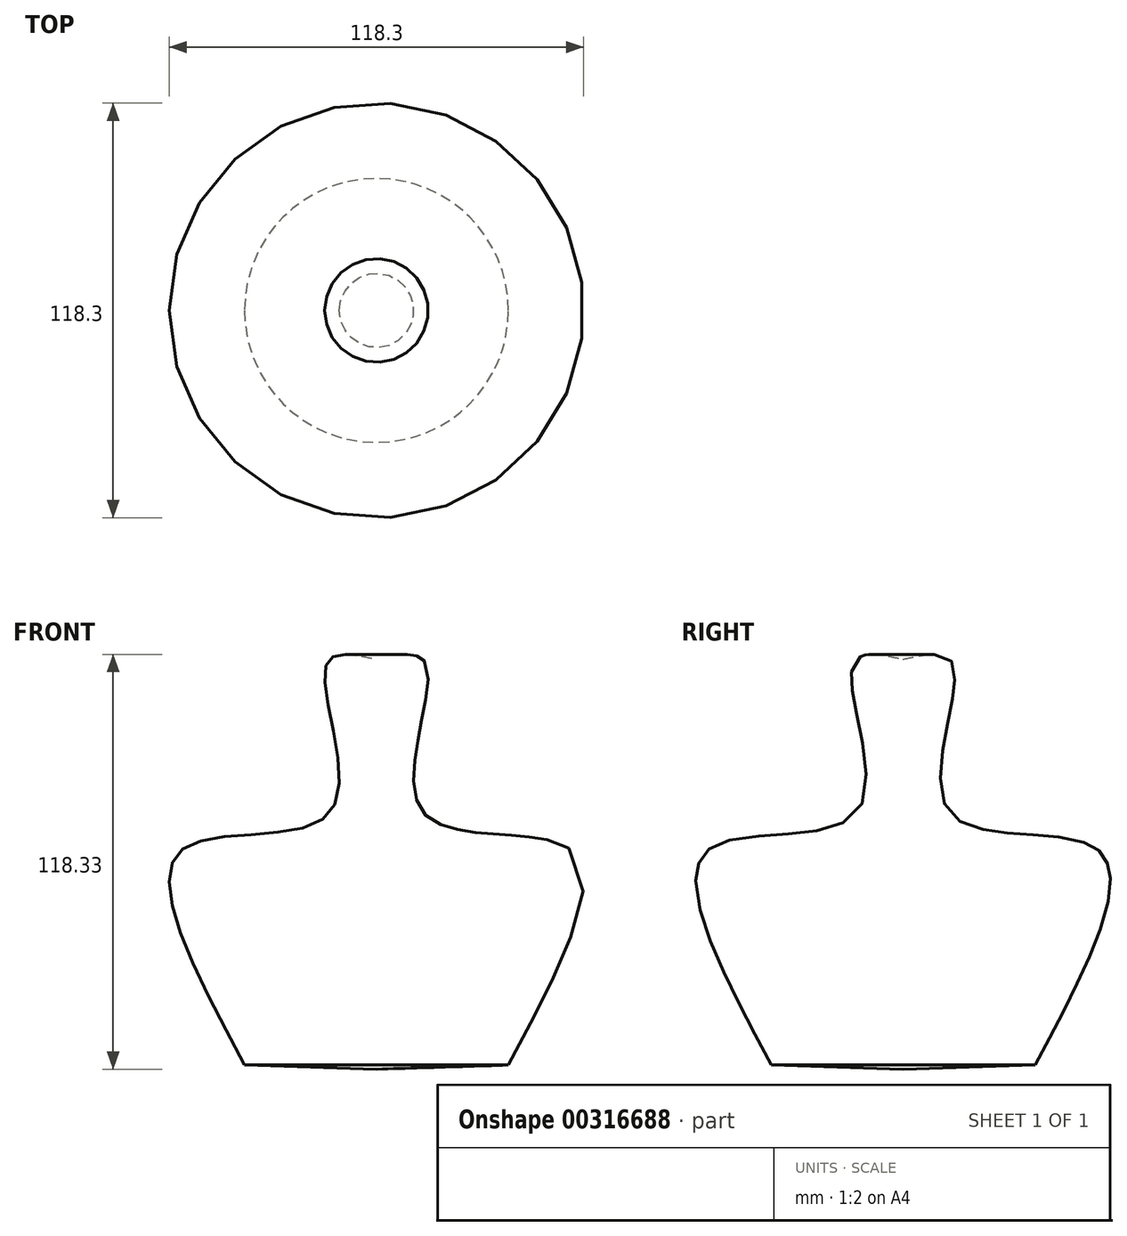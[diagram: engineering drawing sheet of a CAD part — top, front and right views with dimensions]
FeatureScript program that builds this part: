
annotation { "Feature Type Name" : "Feature", "Feature Type Description" : "" }
export const myFeature = defineFeature(function(context is Context, id is Id, definition is map)
    precondition{}
    {
        {
            var Q0;
            Q0=qCreatedBy(makeId("Front.planeOp"),FACE);
            var sketch = newSketch(context, id + "F0", { "sketchPlane" : qUnion([Q0])});
            skFitSpline(sketch, "E0", {"points": [v(-37.65, -61.65) * mm, v(-55.3, 0) * mm, v(-12.94, 10.82) * mm, v(-14.35, 52.48) * mm, v(0, 54.12) * mm], "startDerivative": vector(-133.07, 248.93) * mm, "endDerivative": vector(125.3, -27.6) * mm});
            skLineSegment(sketch, "E1", {"start": v(0, 54.12) * mm, "end": v(0, -62.83) * mm});
            skFitSpline(sketch, "E2", {"points": [v(-37.65, -61.65) * mm, v(0, -62.83) * mm], "startDerivative": vector(37.65, -1.18) * mm, "endDerivative": vector(37.65, -1.18) * mm});
            skSolve(sketch);
        }
        {
            var Q0;
            Q0=qCreatedBy(makeId("Front.planeOp"),FACE);
            var sketch = newSketch(context, id + "F1", { "sketchPlane" : qUnion([Q0])});
            skLineSegment(sketch, "E3", {"start": v(0, 54.36) * mm, "end": v(0, -61.42) * mm, "construction": true});
            skSolve(sketch);
        }
        {
            var Q0;
            Q0 = qSketchRegion(id + "F1", true);
            var Q1;
            Q1 = qSketchRegion(id + "F0", true);
            var Q2;
            Q2=sQuery(id+"F0.wireOp",EDGE,"E1");
            revolve(context, id + "F2", {"entities" : qUnion([Q0, Q1]), "axis" : qUnion([Q2]), "revolveType" : RevolveType.FULL});
        }
    });
